# Revit family: Alcon-14054-S-6-Revit-Family
name_source: partatom
category: Lighting Fixtures
units: mm (PartAtom-declared; Revit-internal decimal feet)

## family parameters
Cut with Voids When Loaded = No
Host = Face
Light Source = Yes
Maintain Annotation Orientation = No
Part Type = Normal
Room Calculation Point = No
Round Connector Dimension = Use Diameter
Shared = No

## types (1)
- Refer To Type Catalog
    Apparent Power = 0 VA
    Brand = Alcon Lighting
    Color Filter = 16777215
    Connector Offset = 0' - 6"
    Default Elevation = 0' - 0"
    Description = Slim Linear Surface Light
    Diffuser Material = SPR - Diffuser
    Dimming Lamp Color Temperature Shift = <None>
    Emit from Line Length = 8' - 0"
    Host Thickness = 1' - 0"
    Housing Material = SPR - Housing
    IES File URL = [IES File URL]
    Lamp = LED
    Left End Cap (disable if necessary for continuous run) = Yes
    Lumens Per Lamp = 0
    Luminaire Depth = 0' - 5 5/8"
    Luminaire Length = 8' - 0"
    Luminaire Width = 0' - 4 1/4"
    Manufacturer = Alcon Lighting
    Model = 14054-S-6
    Number of Lamps = 1
    Photometric Web File = generic
    Plan Symbol = Yes
    Run Length = 8' - 0"
    Specification Sheet URL = https://www.alconlighting.com
    Tilt Angle = 90.00°
    URL = https://www.alconlighting.com
    Wattage Comments = 46

## geometry (parser evidence)
native form markers: Blend x10, Sweep x4
no freeform markers — native parametric forms only
